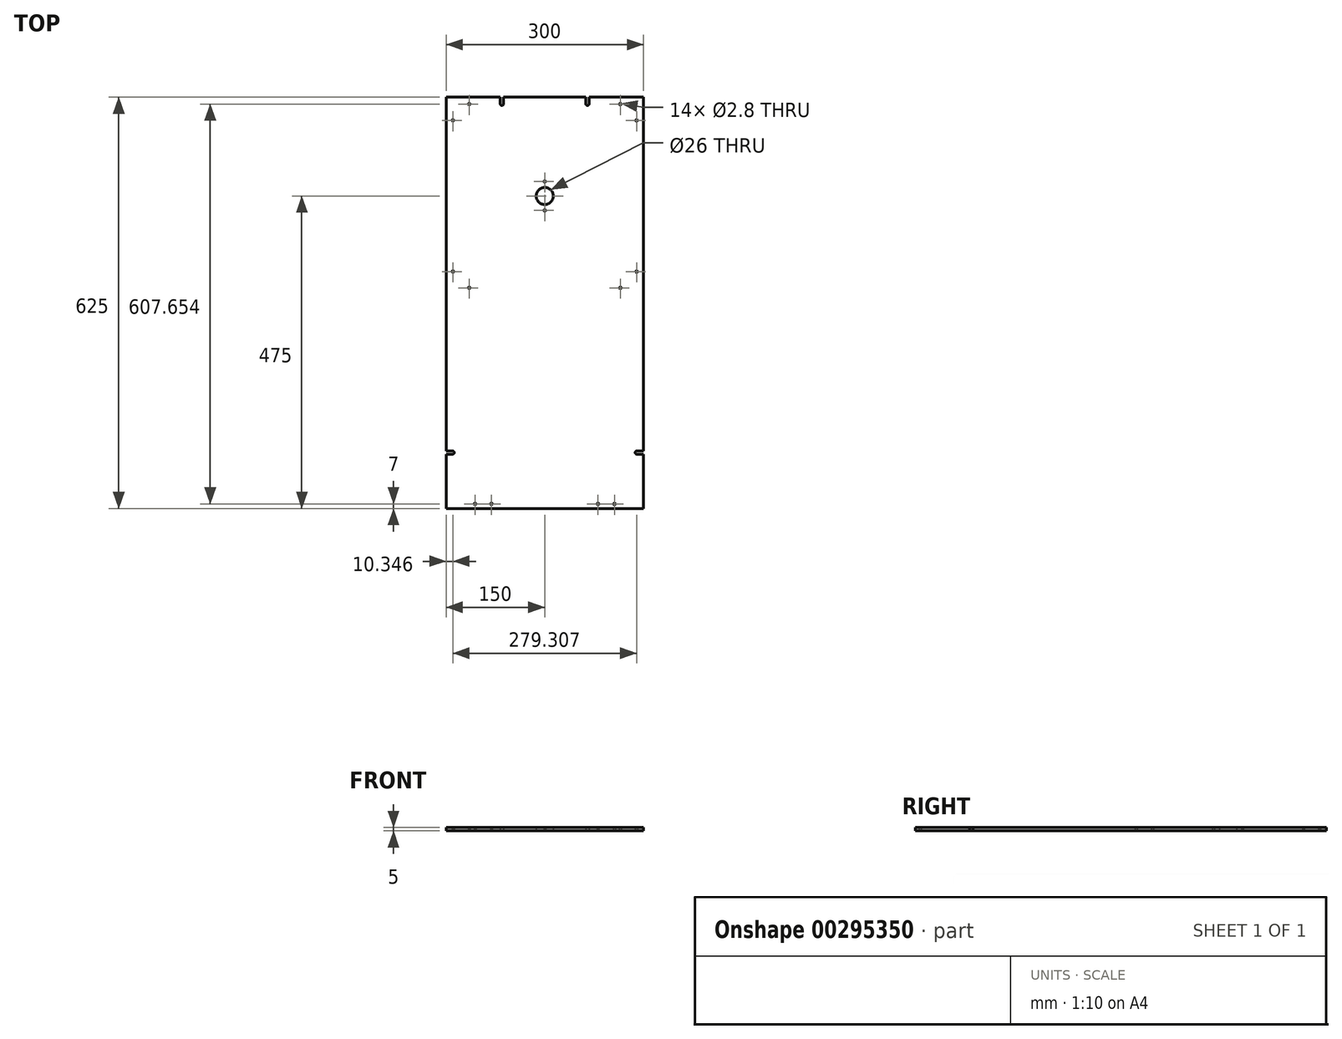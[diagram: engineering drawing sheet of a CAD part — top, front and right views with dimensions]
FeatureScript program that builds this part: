
annotation { "Feature Type Name" : "Feature", "Feature Type Description" : "" }
export const myFeature = defineFeature(function(context is Context, id is Id, definition is map)
    precondition{}
    {
        {
            var Q0;
            Q0=qCreatedBy(makeId("Top.planeOp"),FACE);
            var sketch = newSketch(context, id + "F0", { "sketchPlane" : qUnion([Q0])});
            skLineSegment(sketch, "E0.bottom", {"start": v(0, 625) * mm, "end": v(82.5, 625) * mm});
            skCircle(sketch, "E1", {"center": v(150, 475) * mm, "radius": 13 * mm});
            skCircle(sketch, "E2.1.0", {"center": v(10.35, 589.9) * mm, "radius": 1.4 * mm});
            skCircle(sketch, "E2.1.1", {"center": v(35.1, 614.65) * mm, "radius": 1.4 * mm});
            skCircle(sketch, "E2.3.0", {"center": v(35.1, 335.35) * mm, "radius": 1.4 * mm});
            skCircle(sketch, "E2.3.1", {"center": v(10.35, 360.1) * mm, "radius": 1.4 * mm});
            skCircle(sketch, "E2.5.0", {"center": v(289.65, 360.1) * mm, "radius": 1.4 * mm});
            skCircle(sketch, "E2.5.1", {"center": v(264.9, 335.35) * mm, "radius": 1.4 * mm});
            skCircle(sketch, "E2.7.0", {"center": v(264.9, 614.65) * mm, "radius": 1.4 * mm});
            skCircle(sketch, "E2.7.1", {"center": v(289.65, 589.9) * mm, "radius": 1.4 * mm});
            skArc(sketch, "E3", {"start": v(10, 82.5) * mm, "mid": v(12.5, 85) * mm, "end": v(10, 87.5) * mm});
            skArc(sketch, "E4", {"start": v(82.5, 615) * mm, "mid": v(85, 612.5) * mm, "end": v(87.5, 615) * mm});
            skCircle(sketch, "E5", {"center": v(150, 453) * mm, "radius": 1.4 * mm});
            skCircle(sketch, "E6", {"center": v(44, 7) * mm, "radius": 1.4 * mm});
            skCircle(sketch, "E7", {"center": v(69, 7) * mm, "radius": 1.4 * mm});
            skLineSegment(sketch, "E8", {"start": v(0, 625) * mm, "end": v(0, 87.5) * mm});
            skLineSegment(sketch, "E9", {"start": v(300, 0) * mm, "end": v(300, 82.5) * mm});
            skLineSegment(sketch, "E10", {"start": v(10, 82.5) * mm, "end": v(0, 82.5) * mm});
            skLineSegment(sketch, "E11", {"start": v(10, 87.5) * mm, "end": v(0, 87.5) * mm});
            skLineSegment(sketch, "E12", {"start": v(82.5, 615) * mm, "end": v(82.5, 625) * mm});
            skLineSegment(sketch, "E13", {"start": v(87.5, 615) * mm, "end": v(87.5, 625) * mm});
            skLineSegment(sketch, "E14.trimOffspring", {"start": v(0, 82.5) * mm, "end": v(0, 0) * mm});
            skLineSegment(sketch, "E15.trimOffspring", {"start": v(87.5, 625) * mm, "end": v(212.5, 625) * mm});
            skLineSegment(sketch, "E16.MirrorCS", {"start": v(290, 82.5) * mm, "end": v(300, 82.5) * mm});
            skLineSegment(sketch, "E17.MirrorCS", {"start": v(290, 87.5) * mm, "end": v(300, 87.5) * mm});
            skLineSegment(sketch, "E18.MirrorCS", {"start": v(217.5, 615) * mm, "end": v(217.5, 625) * mm});
            skLineSegment(sketch, "E19.MirrorCS", {"start": v(212.5, 615) * mm, "end": v(212.5, 625) * mm});
            skLineSegment(sketch, "E20.trimOffspring", {"start": v(217.5, 625) * mm, "end": v(300, 625) * mm});
            skLineSegment(sketch, "E21.trimOffspring", {"start": v(300, 87.5) * mm, "end": v(300, 625) * mm});
            skCircle(sketch, "E22.MirrorC", {"center": v(150, 497) * mm, "radius": 1.4 * mm});
            skArc(sketch, "E23.MirrorCS", {"start": v(290, 82.5) * mm, "mid": v(287.5, 85) * mm, "end": v(290, 87.5) * mm});
            skArc(sketch, "E24.MirrorCS", {"start": v(217.5, 615) * mm, "mid": v(215, 612.5) * mm, "end": v(212.5, 615) * mm});
            skCircle(sketch, "E25.MirrorC", {"center": v(231, 7) * mm, "radius": 1.4 * mm});
            skCircle(sketch, "E26.MirrorC", {"center": v(256, 7) * mm, "radius": 1.4 * mm});
            skLineSegment(sketch, "E27", {"start": v(0, 0) * mm, "end": v(300, 0) * mm});
            skSolve(sketch);
        }
        {
            var Q0;
            Q0=makeQuery(id+"F0.imprint","IMPRINT",FACE,{"disambiguationData":[TD([[makeQuery(id+"F0.imprint","IMPRINT",EDGE,{"derivedFrom":sQuery(id+"F0.wireOp",EDGE,"E0.bottom")}),-1.0]])]});
            extrude(context, id + "F1", {"entities" : qUnion([Q0]), "depth" : 5 * mm});
        }
    });
